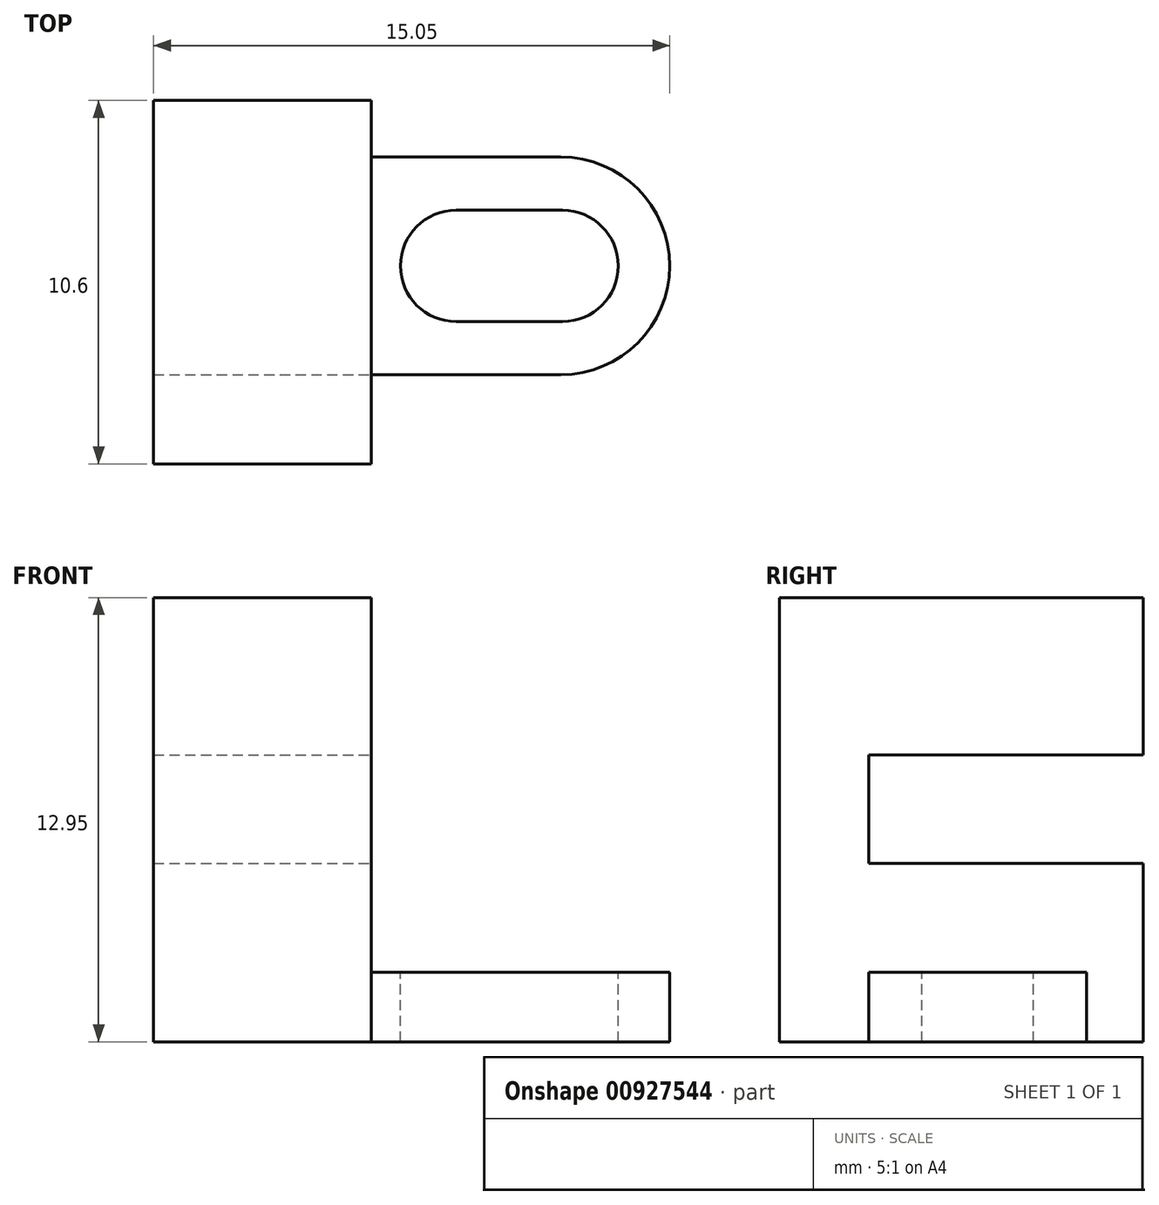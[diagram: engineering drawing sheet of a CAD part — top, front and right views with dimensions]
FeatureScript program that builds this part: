
annotation { "Feature Type Name" : "Feature", "Feature Type Description" : "" }
export const myFeature = defineFeature(function(context is Context, id is Id, definition is map)
    precondition{}
    {
        {
            var Q0;
            Q0=qCreatedBy(makeId("Right.planeOp"),FACE);
            var sketch = newSketch(context, id + "F0", { "sketchPlane" : qUnion([Q0])});
            skLineSegment(sketch, "E0.bottom", {"start": v(0, 12.95) * mm, "end": v(10.6, 12.95) * mm});
            skLineSegment(sketch, "E0.top", {"start": v(0, 0) * mm, "end": v(10.6, 0) * mm});
            skLineSegment(sketch, "E0.left", {"start": v(0, 12.95) * mm, "end": v(0, 0) * mm});
            skLineSegment(sketch, "E0.right", {"start": v(10.6, 12.95) * mm, "end": v(10.6, 0) * mm});
            skSolve(sketch);
        }
        {
            var Q0;
            Q0 = qSketchRegion(id + "F0", true);
            extrude(context, id + "F1", {"entities" : qUnion([Q0]), "oppositeDirection" : true, "depth" : 6.35 * mm, "offsetDistance" : 25 * mm});
        }
        {
            var Q0;
            Q0=makeQuery(id+"F1.opExtrude","CAP_FACE",FACE,{"disambiguationData":[OSD([sQuery(id+"F0.wireOp",EDGE,"E0.bottom"),sQuery(id+"F0.wireOp",EDGE,"E0.top"),sQuery(id+"F0.wireOp",EDGE,"E0.left"),sQuery(id+"F0.wireOp",EDGE,"E0.right")])],"isStart":true});
            var sketch = newSketch(context, id + "F2", { "sketchPlane" : qUnion([Q0])});
            skLineSegment(sketch, "E1.bottom", {"start": v(10.6, 8.37) * mm, "end": v(2.6, 8.37) * mm});
            skLineSegment(sketch, "E1.top", {"start": v(10.6, 5.2) * mm, "end": v(2.6, 5.2) * mm});
            skLineSegment(sketch, "E1.left", {"start": v(10.6, 8.37) * mm, "end": v(10.6, 5.2) * mm});
            skLineSegment(sketch, "E1.right", {"start": v(2.6, 8.37) * mm, "end": v(2.6, 5.2) * mm});
            skSolve(sketch);
        }
        {
            var Q0;
            Q0 = qSketchRegion(id + "F2", true);
            extrude(context, id + "F3", {"entities" : qUnion([Q0]), "operationType" : NewBodyOperationType.REMOVE, "endBound" : BoundingType.THROUGH_ALL, "oppositeDirection" : true, "depth" : 25 * mm, "offsetDistance" : 25 * mm});
        }
        {
            var Q0;
            Q0=makeQuery(id+"F1.opExtrude","CAP_FACE",FACE,{"disambiguationData":[OSD([sQuery(id+"F0.wireOp",EDGE,"E0.bottom"),sQuery(id+"F0.wireOp",EDGE,"E0.top"),sQuery(id+"F0.wireOp",EDGE,"E0.left"),sQuery(id+"F0.wireOp",EDGE,"E0.right")])],"isStart":true});
            var sketch = newSketch(context, id + "F4", { "sketchPlane" : qUnion([Q0])});
            skLineSegment(sketch, "E2.bottom", {"start": v(2.6, 0) * mm, "end": v(8.95, 0) * mm});
            skLineSegment(sketch, "E2.top", {"start": v(2.6, 2.03) * mm, "end": v(8.95, 2.03) * mm});
            skLineSegment(sketch, "E2.left", {"start": v(2.6, 0) * mm, "end": v(2.6, 2.03) * mm});
            skLineSegment(sketch, "E2.right", {"start": v(8.95, 0) * mm, "end": v(8.95, 2.03) * mm});
            skSolve(sketch);
        }
        {
            var Q0;
            Q0 = qSketchRegion(id + "F4", true);
            extrude(context, id + "F5", {"entities" : qUnion([Q0]), "operationType" : NewBodyOperationType.ADD, "depth" : 8.7 * mm, "offsetDistance" : 25 * mm});
        }
        {
            var Q0;
            Q0=makeQuery(id+"F5.opExtrude","CAP_EDGE",EDGE,{"disambiguationData":[OSD([sQuery(id+"F4.wireOp",EDGE,"E2.left")])],"isStart":false});
            var Q1;
            Q1=makeQuery(id+"F5.opExtrude","CAP_EDGE",EDGE,{"disambiguationData":[OSD([sQuery(id+"F4.wireOp",EDGE,"E2.right")])],"isStart":false});
            fillet(context, id + "F6", {"entities" : qUnion([Q0, Q1]), "radius" : 3.17 * mm, "tangentPropagation" : true, "allowEdgeOverflow" : false});
        }
        {
            var Q0;
            Q0=qCreatedBy(makeId("Right.planeOp"),FACE);
            cPlane(context, id + "F7", {"entities" : qUnion([Q0]), "cplaneType" : CPlaneType.OFFSET, "offset" : (6.35 / 2) * mm, "oppositeDirection" : true, "width" : 150 * mm, "height" : 150 * mm});
        }
        {
            var Q0;
            Q0=makeQuery(id+"F5.opExtrude","SWEPT_FACE",FACE,{"disambiguationData":[OSD([sQuery(id+"F4.wireOp",EDGE,"E2.top")])]});
            var sketch = newSketch(context, id + "F8", { "sketchPlane" : qUnion([Q0])});
            skArc(sketch, "E3", {"start": v(5.57, 4.15) * mm, "mid": v(7.2, 5.78) * mm, "end": v(5.57, 7.4) * mm});
            skLineSegment(sketch, "E4", {"start": v(10.71, 5.77) * mm, "end": v(-10.54, 5.77) * mm, "construction": true});
            skPoint(sketch, "E4.startSnap0", {"position": v(8.7, 5.77) * mm});
            skLineSegment(sketch, "E5", {"start": v(2.47, 7.4) * mm, "end": v(5.57, 7.4) * mm});
            skLineSegment(sketch, "E6", {"start": v(2.47, 4.15) * mm, "end": v(5.57, 4.15) * mm});
            skArc(sketch, "E7.trimOffspring", {"start": v(2.47, 7.4) * mm, "mid": v(0.84, 5.78) * mm, "end": v(2.47, 4.15) * mm});
            skSolve(sketch);
        }
        {
            var Q0;
            Q0 = qSketchRegion(id + "F8", true);
            extrude(context, id + "F9", {"entities" : qUnion([Q0]), "operationType" : NewBodyOperationType.REMOVE, "endBound" : BoundingType.THROUGH_ALL, "oppositeDirection" : true, "depth" : 25 * mm, "offsetDistance" : 25 * mm});
        }
    });
